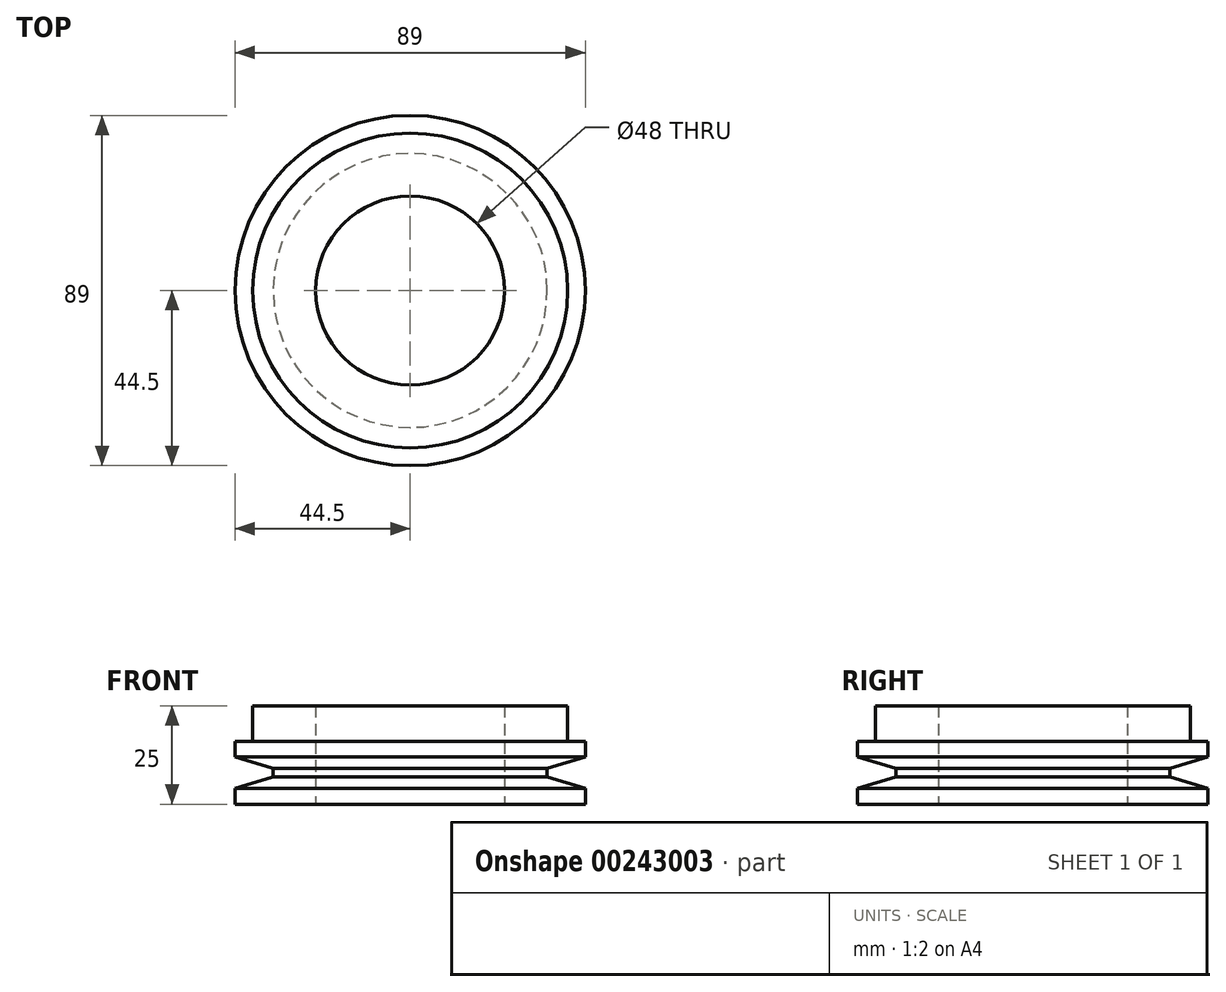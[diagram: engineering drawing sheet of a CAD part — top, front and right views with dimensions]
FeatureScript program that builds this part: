
annotation { "Feature Type Name" : "Feature", "Feature Type Description" : "" }
export const myFeature = defineFeature(function(context is Context, id is Id, definition is map)
    precondition{}
    {
        {
            var Q0;
            Q0=qCreatedBy(makeId("Top.planeOp"),FACE);
            var sketch = newSketch(context, id + "F0", { "sketchPlane" : qUnion([Q0])});
            skCircle(sketch, "E0", {"center": v(0, 0) * mm, "radius": 44.5 * mm});
            skCircle(sketch, "E1", {"center": v(0, 0) * mm, "radius": 40 * mm});
            skCircle(sketch, "E2", {"center": v(0, 0) * mm, "radius": 24 * mm});
            skSolve(sketch);
        }
        {
            var Q0;
            Q0=makeQuery(id+"F0.imprint","IMPRINT",FACE,{"disambiguationData":[TD([[makeQuery(id+"F0.imprint","IMPRINT",EDGE,{"derivedFrom":sQuery(id+"F0.wireOp",EDGE,"E0")}),1.0]])]});
            var Q1;
            Q1=makeQuery(id+"F0.imprint","IMPRINT",FACE,{"disambiguationData":[TD([[makeQuery(id+"F0.imprint","IMPRINT",EDGE,{"derivedFrom":sQuery(id+"F0.wireOp",EDGE,"E1")}),-1.0]])]});
            var Q2;
            Q2=makeQuery(id+"F0.imprint","IMPRINT",FACE,{"disambiguationData":[TD([[makeQuery(id+"F0.imprint","IMPRINT",EDGE,{"derivedFrom":sQuery(id+"F0.wireOp",EDGE,"E1")}),1.0]])]});
            extrude(context, id + "F1", {"entities" : qUnion([Q0, Q1, Q2]), "depth" : 16 * mm});
        }
        {
            var Q0;
            Q0=makeQuery(id+"F0.imprint","IMPRINT",FACE,{"disambiguationData":[TD([[makeQuery(id+"F0.imprint","IMPRINT",EDGE,{"derivedFrom":sQuery(id+"F0.wireOp",EDGE,"E1")}),1.0]])]});
            extrude(context, id + "F2", {"entities" : qUnion([Q0]), "operationType" : NewBodyOperationType.ADD, "depth" : 25 * mm});
        }
        {
            var Q0;
            Q0=qCreatedBy(makeId("Front.planeOp"),FACE);
            var sketch = newSketch(context, id + "F3", { "sketchPlane" : qUnion([Q0])});
            skLineSegment(sketch, "E3", {"start": v(-44.5, 12) * mm, "end": v(-34.8, 9.03) * mm});
            skLineSegment(sketch, "E4", {"start": v(-34.8, 6.97) * mm, "end": v(-44.5, 4) * mm});
            skLineSegment(sketch, "E5", {"start": v(-44.5, 4) * mm, "end": v(-44.5, 12) * mm});
            skLineSegment(sketch, "E6", {"start": v(-34.8, 9.03) * mm, "end": v(-34.8, 6.97) * mm});
            skPoint(sketch, "E7", {"position": v(-44.5, 8) * mm});
            skLineSegment(sketch, "E8", {"start": v(0, 0) * mm, "end": v(0, -11.25) * mm});
            skSolve(sketch);
        }
        {
            var Q0;
            Q0 = qSketchRegion(id + "F3", true);
            var Q1;
            Q1=sQuery(id+"F3.wireOp",EDGE,"E8");
            revolve(context, id + "F4", {"operationType" : NewBodyOperationType.REMOVE, "entities" : qUnion([Q0]), "axis" : qUnion([Q1]), "revolveType" : RevolveType.FULL, "oppositeDirection" : true});
        }
    });
